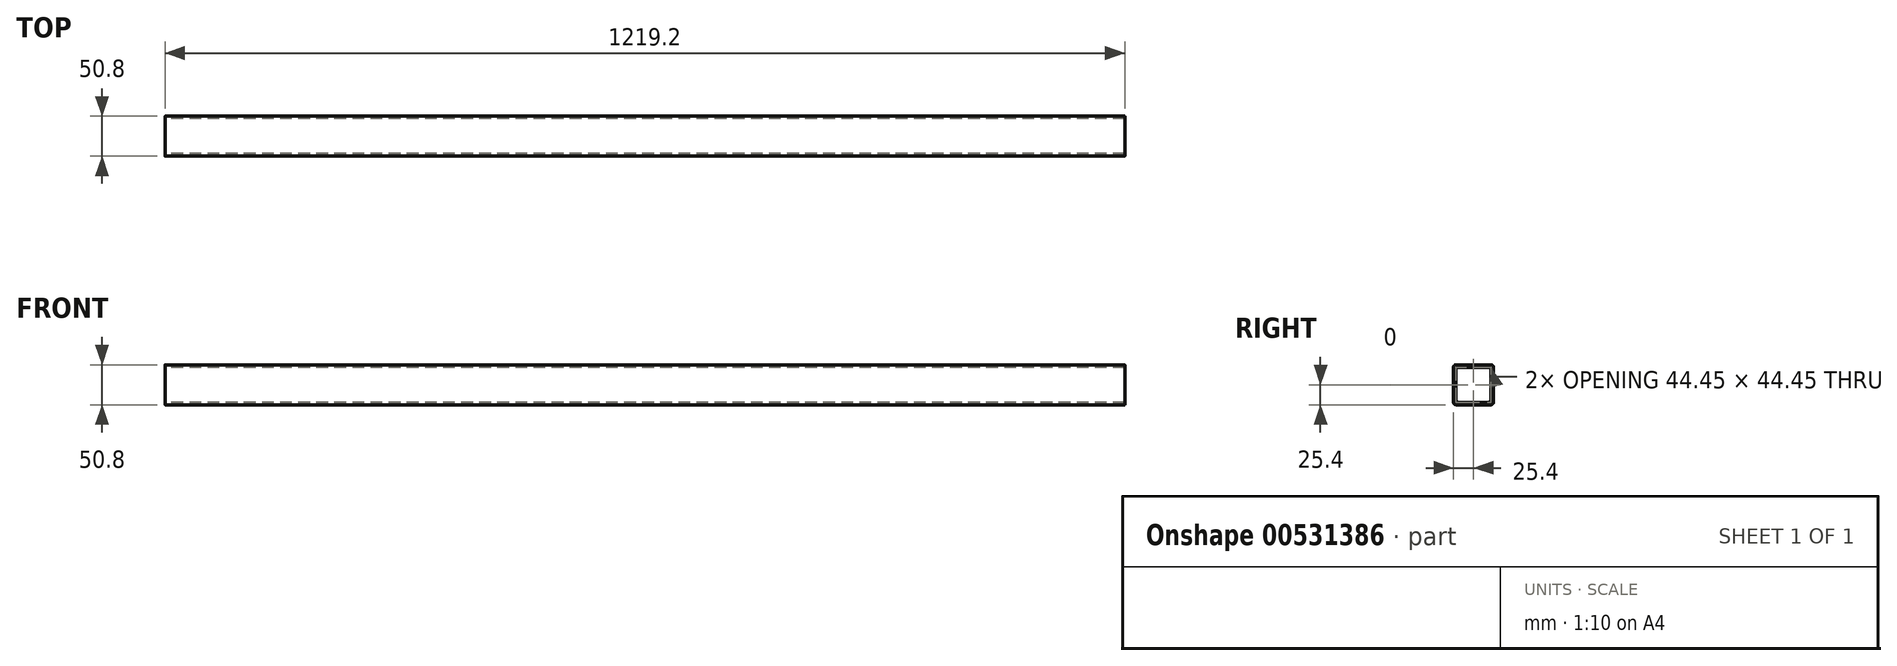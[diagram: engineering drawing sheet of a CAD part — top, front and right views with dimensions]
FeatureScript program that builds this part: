
annotation { "Feature Type Name" : "Feature", "Feature Type Description" : "" }
export const myFeature = defineFeature(function(context is Context, id is Id, definition is map)
    precondition{}
    {
        {
            var Q0;
            Q0=qCreatedBy(makeId("Right.planeOp"),FACE);
            var sketch = newSketch(context, id + "F0", { "sketchPlane" : qUnion([Q0])});
            skLineSegment(sketch, "E0.bottom", {"start": v(22.23, -25.4) * mm, "end": v(-22.23, -25.4) * mm});
            skLineSegment(sketch, "E0.top", {"start": v(22.23, 25.4) * mm, "end": v(-22.23, 25.4) * mm});
            skLineSegment(sketch, "E0.left", {"start": v(25.4, -22.22) * mm, "end": v(25.4, 22.23) * mm});
            skLineSegment(sketch, "E0.right", {"start": v(-25.4, -22.22) * mm, "end": v(-25.4, 22.23) * mm});
            skPoint(sketch, "E0.middle", {"position": v(0, 0) * mm});
            skLineSegment(sketch, "E1.bottom", {"start": v(19.05, -22.22) * mm, "end": v(-19.05, -22.23) * mm});
            skLineSegment(sketch, "E1.top", {"start": v(19.05, 22.23) * mm, "end": v(-19.05, 22.22) * mm});
            skLineSegment(sketch, "E1.left", {"start": v(22.23, -19.05) * mm, "end": v(22.22, 19.05) * mm});
            skLineSegment(sketch, "E1.right", {"start": v(-22.22, -19.05) * mm, "end": v(-22.23, 19.05) * mm});
            skPoint(sketch, "E2.visualSharp", {"position": v(-22.23, 22.22) * mm});
            skArc(sketch, "E2.filletArc", {"start": v(-19.05, 22.22) * mm, "mid": v(-21.3, 21.3) * mm, "end": v(-22.23, 19.05) * mm});
            skPoint(sketch, "E3.visualSharp", {"position": v(22.22, 22.23) * mm});
            skArc(sketch, "E3.filletArc", {"start": v(22.22, 19.05) * mm, "mid": v(21.3, 21.3) * mm, "end": v(19.05, 22.23) * mm});
            skPoint(sketch, "E4.visualSharp", {"position": v(22.23, -22.22) * mm});
            skArc(sketch, "E4.filletArc", {"start": v(19.05, -22.22) * mm, "mid": v(21.3, -21.3) * mm, "end": v(22.23, -19.05) * mm});
            skPoint(sketch, "E5.visualSharp", {"position": v(-22.22, -22.23) * mm});
            skArc(sketch, "E5.filletArc", {"start": v(-22.22, -19.05) * mm, "mid": v(-21.3, -21.3) * mm, "end": v(-19.05, -22.23) * mm});
            skPoint(sketch, "E6.visualSharp", {"position": v(-25.4, -25.4) * mm});
            skArc(sketch, "E6.filletArc", {"start": v(-25.4, -22.22) * mm, "mid": v(-24.47, -24.47) * mm, "end": v(-22.23, -25.4) * mm});
            skPoint(sketch, "E7.visualSharp", {"position": v(25.4, -25.4) * mm});
            skArc(sketch, "E7.filletArc", {"start": v(22.23, -25.4) * mm, "mid": v(24.47, -24.47) * mm, "end": v(25.4, -22.22) * mm});
            skPoint(sketch, "E8.visualSharp", {"position": v(25.4, 25.4) * mm});
            skArc(sketch, "E8.filletArc", {"start": v(25.4, 22.23) * mm, "mid": v(24.47, 24.47) * mm, "end": v(22.23, 25.4) * mm});
            skPoint(sketch, "E9.visualSharp", {"position": v(-25.4, 25.4) * mm});
            skArc(sketch, "E9.filletArc", {"start": v(-22.23, 25.4) * mm, "mid": v(-24.47, 24.47) * mm, "end": v(-25.4, 22.23) * mm});
            skSolve(sketch);
        }
        {
            var Q0;
            Q0 = qSketchRegion(id + "F0", true);
            extrude(context, id + "F1", {"entities" : qUnion([Q0]), "endBound" : BoundingType.SYMMETRIC, "depth" : 1219.2 * mm, "offsetDistance" : 25.4 * mm});
        }
    });
